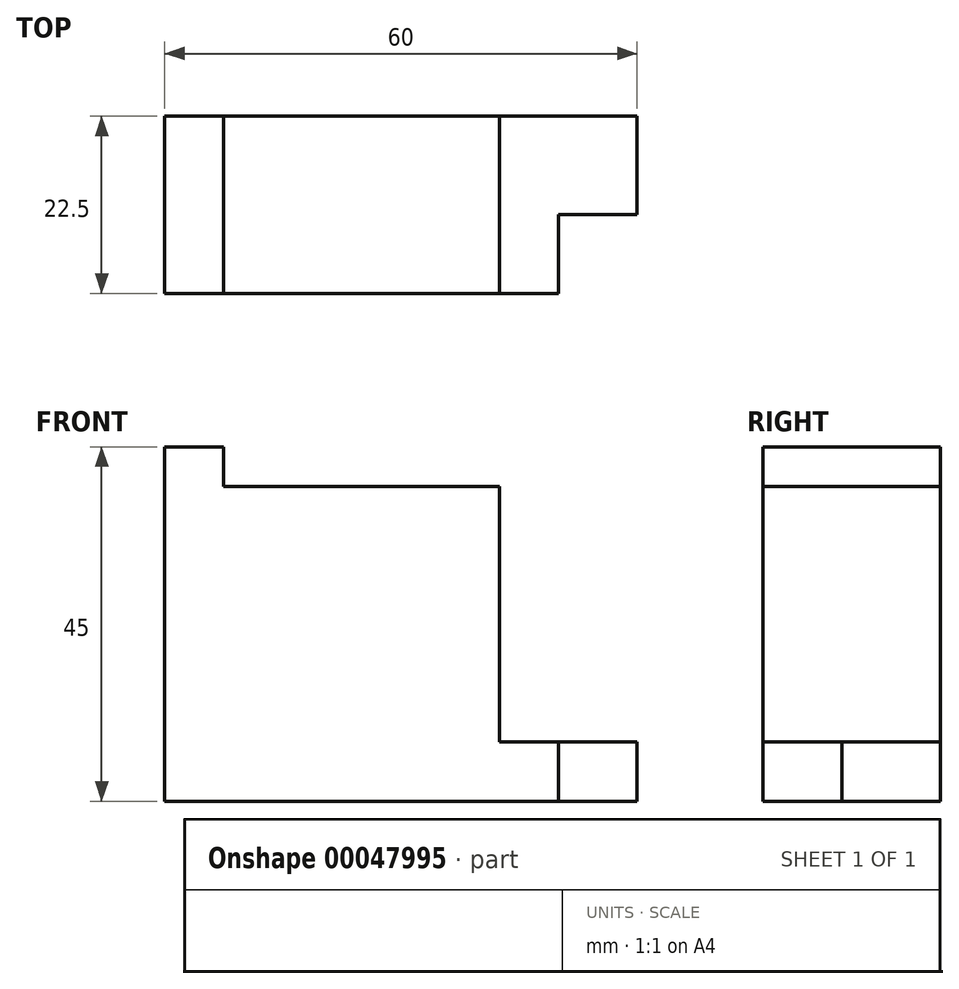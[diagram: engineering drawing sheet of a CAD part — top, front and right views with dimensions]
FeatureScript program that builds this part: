
annotation { "Feature Type Name" : "Feature", "Feature Type Description" : "" }
export const myFeature = defineFeature(function(context is Context, id is Id, definition is map)
    precondition{}
    {
        {
            var Q0;
            Q0=qCreatedBy(makeId("Front.planeOp"),FACE);
            var sketch = newSketch(context, id + "F0", { "sketchPlane" : qUnion([Q0])});
            skLineSegment(sketch, "E0", {"start": v(0, 0) * mm, "end": v(0, 45) * mm});
            skLineSegment(sketch, "E1", {"start": v(0, 45) * mm, "end": v(7.5, 45) * mm});
            skLineSegment(sketch, "E2", {"start": v(7.5, 45) * mm, "end": v(7.5, 40) * mm});
            skLineSegment(sketch, "E3", {"start": v(7.5, 40) * mm, "end": v(42.5, 40) * mm});
            skLineSegment(sketch, "E4", {"start": v(42.5, 40) * mm, "end": v(42.5, 7.5) * mm});
            skLineSegment(sketch, "E5", {"start": v(42.5, 7.5) * mm, "end": v(60, 7.5) * mm});
            skLineSegment(sketch, "E6", {"start": v(60, 7.5) * mm, "end": v(60, 0) * mm});
            skLineSegment(sketch, "E7", {"start": v(60, 0) * mm, "end": v(0, 0) * mm});
            skSolve(sketch);
        }
        {
            var Q0;
            Q0=makeQuery(id+"F0.imprint","IMPRINT",FACE,{"disambiguationData":[TD([[makeQuery(id+"F0.imprint","IMPRINT",EDGE,{"derivedFrom":sQuery(id+"F0.wireOp",EDGE,"E0")}),-1.0]])]});
            extrude(context, id + "F1", {"entities" : qUnion([Q0]), "oppositeDirection" : true, "depth" : 22.5 * mm});
        }
        {
            var Q0;
            Q0=makeQuery(id+"F1.opExtrude","SWEPT_FACE",FACE,{"disambiguationData":[OSD([sQuery(id+"F0.wireOp",EDGE,"E5")])]});
            var sketch = newSketch(context, id + "F2", { "sketchPlane" : qUnion([Q0])});
            skLineSegment(sketch, "E8.bottom", {"start": v(60, 0) * mm, "end": v(50, 0) * mm});
            skLineSegment(sketch, "E8.top", {"start": v(60, 10) * mm, "end": v(50, 10) * mm});
            skLineSegment(sketch, "E8.left", {"start": v(60, 0) * mm, "end": v(60, 10) * mm});
            skLineSegment(sketch, "E8.right", {"start": v(50, 0) * mm, "end": v(50, 10) * mm});
            skSolve(sketch);
        }
        {
            var Q0;
            Q0=makeQuery(id+"F2.imprint","IMPRINT",FACE,{"disambiguationData":[TD([[makeQuery(id+"F2.imprint","IMPRINT",EDGE,{"derivedFrom":sQuery(id+"F2.wireOp",EDGE,"E8.bottom")}),1.0]])]});
            extrude(context, id + "F3", {"entities" : qUnion([Q0]), "operationType" : NewBodyOperationType.REMOVE, "endBound" : BoundingType.UP_TO_NEXT, "oppositeDirection" : true, "depth" : 25 * mm});
        }
    });
